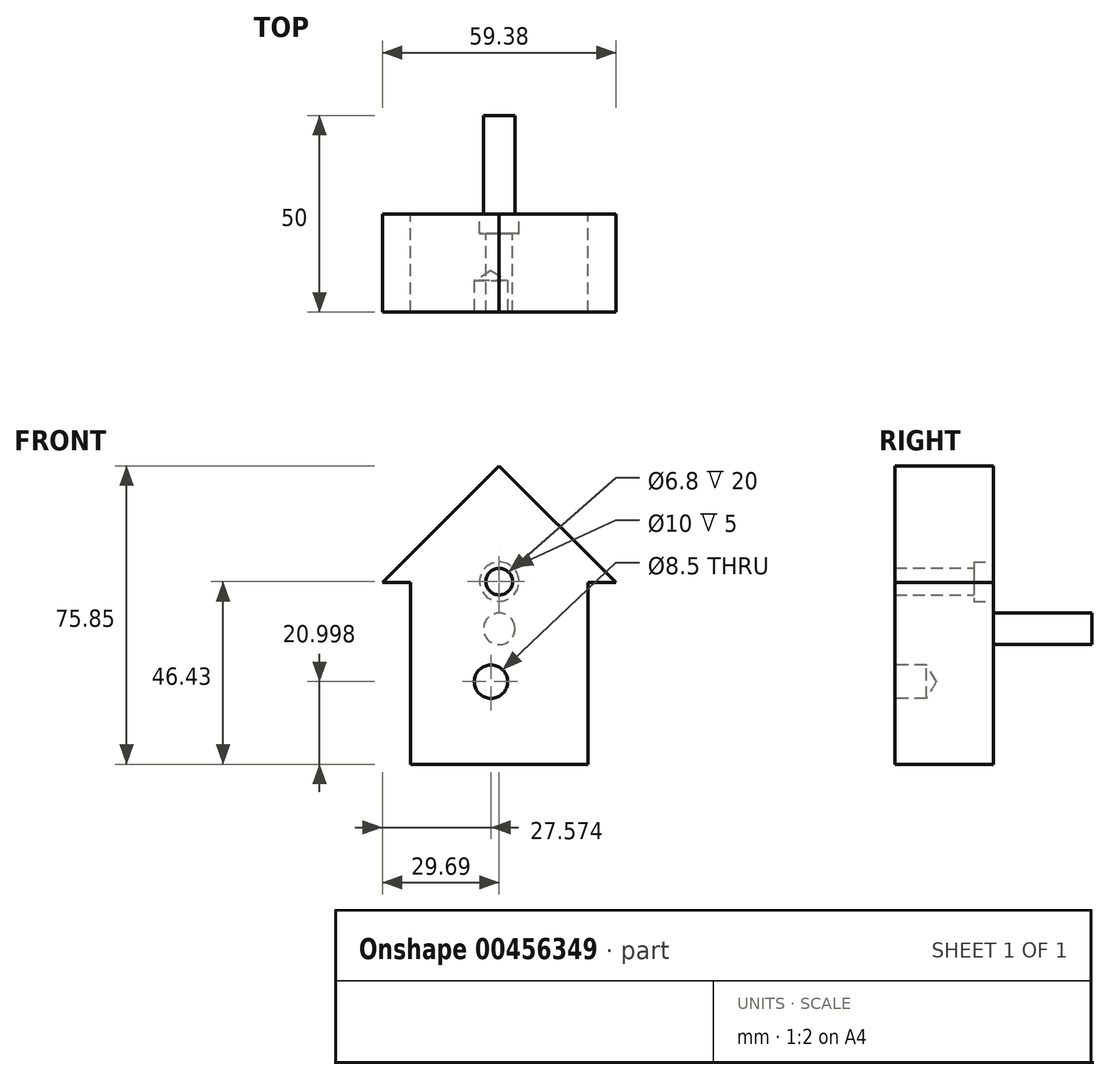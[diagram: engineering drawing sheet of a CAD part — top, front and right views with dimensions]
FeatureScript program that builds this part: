
annotation { "Feature Type Name" : "Feature", "Feature Type Description" : "" }
export const myFeature = defineFeature(function(context is Context, id is Id, definition is map)
    precondition{}
    {
        {
            var Q0;
            Q0=qCreatedBy(makeId("Front.planeOp"),FACE);
            var sketch = newSketch(context, id + "F0", { "sketchPlane" : qUnion([Q0])});
            skLineSegment(sketch, "E0", {"start": v(-22.57, -26.69) * mm, "end": v(22.57, -26.69) * mm});
            skLineSegment(sketch, "E1", {"start": v(22.57, -26.69) * mm, "end": v(22.57, 19.47) * mm});
            skLineSegment(sketch, "E2", {"start": v(22.57, 19.47) * mm, "end": v(29.69, 19.47) * mm});
            skLineSegment(sketch, "E3", {"start": v(29.69, 19.47) * mm, "end": v(0, 49.16) * mm});
            skLineSegment(sketch, "E4", {"start": v(0, 49.16) * mm, "end": v(-29.69, 19.47) * mm});
            skLineSegment(sketch, "E5", {"start": v(-29.69, 19.47) * mm, "end": v(-22.57, 19.47) * mm});
            skLineSegment(sketch, "E6", {"start": v(-22.57, 19.47) * mm, "end": v(-22.57, -26.69) * mm});
            skSolve(sketch);
        }
        {
            var Q0;
            Q0 = qSketchRegion(id + "F0", true);
            extrude(context, id + "F1", {"entities" : qUnion([Q0]), "depth" : 25 * mm});
        }
        {
            var Q0;
            Q0=makeQuery(id+"F1.opExtrude","CAP_FACE",FACE,{"disambiguationData":[OSD([sQuery(id+"F0.wireOp",EDGE,"E0"),sQuery(id+"F0.wireOp",EDGE,"E1"),sQuery(id+"F0.wireOp",EDGE,"E2"),sQuery(id+"F0.wireOp",EDGE,"E3"),sQuery(id+"F0.wireOp",EDGE,"E4"),sQuery(id+"F0.wireOp",EDGE,"E5"),sQuery(id+"F0.wireOp",EDGE,"E6")])],"isStart":true});
            var sketch = newSketch(context, id + "F2", { "sketchPlane" : qUnion([Q0])});
            skCircle(sketch, "E7", {"center": v(0, 7.72) * mm, "radius": 4 * mm});
            skSolve(sketch);
        }
        {
            var Q0;
            Q0 = qSketchRegion(id + "F2", true);
            extrude(context, id + "F3", {"entities" : qUnion([Q0]), "operationType" : NewBodyOperationType.ADD, "depth" : 25 * mm});
        }
        {
            var Q0;
            Q0=makeQuery(id+"F1.opExtrude","CAP_FACE",FACE,{"disambiguationData":[OSD([sQuery(id+"F0.wireOp",EDGE,"E0"),sQuery(id+"F0.wireOp",EDGE,"E1"),sQuery(id+"F0.wireOp",EDGE,"E2"),sQuery(id+"F0.wireOp",EDGE,"E3"),sQuery(id+"F0.wireOp",EDGE,"E4"),sQuery(id+"F0.wireOp",EDGE,"E5"),sQuery(id+"F0.wireOp",EDGE,"E6")])],"isStart":true});
            var sketch = newSketch(context, id + "F4", { "sketchPlane" : qUnion([Q0])});
            skCircle(sketch, "E8", {"center": v(0, 19.74) * mm, "radius": 7.9 * mm});
            skSolve(sketch);
        }
        {
            var Q0;
            Q0=sQuery(id+"F4.wireOp",VERTEX,"E8.center");
            var Q1;
            Q1=makeQuery(id+"F1.opExtrude","SWEPT_BODY",BODY,{"disambiguationData":[OSD([sQuery(id+"F0.wireOp",EDGE,"E0"),sQuery(id+"F0.wireOp",EDGE,"E1"),sQuery(id+"F0.wireOp",EDGE,"E2"),sQuery(id+"F0.wireOp",EDGE,"E3"),sQuery(id+"F0.wireOp",EDGE,"E4"),sQuery(id+"F0.wireOp",EDGE,"E5"),sQuery(id+"F0.wireOp",EDGE,"E6")])]});
            hole(context, id + "F5", {"style" : HoleStyle.C_BORE, "endStyle" : HoleEndStyle.THROUGH, "holeDiameter" : 6.8 * mm, "cBoreDiameter" : 10 * mm, "cBoreDepth" : 5 * mm, "majorDiameter" : 5 * mm, "isTappedThrough" : true, "tappedDepth" : 12 * mm, "tapClearance" : 3, "locations" : qUnion([Q0]), "scope" : qUnion([Q1])});
        }
        {
            var Q0;
            Q0=makeQuery(id+"F1.opExtrude","CAP_FACE",FACE,{"disambiguationData":[OSD([sQuery(id+"F0.wireOp",EDGE,"E0"),sQuery(id+"F0.wireOp",EDGE,"E1"),sQuery(id+"F0.wireOp",EDGE,"E2"),sQuery(id+"F0.wireOp",EDGE,"E3"),sQuery(id+"F0.wireOp",EDGE,"E4"),sQuery(id+"F0.wireOp",EDGE,"E5"),sQuery(id+"F0.wireOp",EDGE,"E6")])],"isStart":false});
            var sketch = newSketch(context, id + "F6", { "sketchPlane" : qUnion([Q0])});
            skCircle(sketch, "E9", {"center": v(-2.12, -5.7) * mm, "radius": 6 * mm});
            skCircle(sketch, "E10", {"center": v(-13.43, 9) * mm, "radius": 4.63 * mm});
            skSolve(sketch);
        }
        {
            var Q0;
            Q0=sQuery(id+"F6.wireOp",VERTEX,"E9.center");
            var Q1;
            Q1=makeQuery(id+"F1.opExtrude","SWEPT_BODY",BODY,{"disambiguationData":[OSD([sQuery(id+"F0.wireOp",EDGE,"E0"),sQuery(id+"F0.wireOp",EDGE,"E1"),sQuery(id+"F0.wireOp",EDGE,"E2"),sQuery(id+"F0.wireOp",EDGE,"E3"),sQuery(id+"F0.wireOp",EDGE,"E4"),sQuery(id+"F0.wireOp",EDGE,"E5"),sQuery(id+"F0.wireOp",EDGE,"E6")])]});
            hole(context, id + "F7", {"style" : HoleStyle.C_SINK, "endStyle" : HoleEndStyle.BLIND, "holeDiameter" : 8.5 * mm, "cSinkDiameter" : 8.5 * mm, "cSinkAngle" : 82 * degree, "majorDiameter" : 5 * mm, "holeDepth" : 8 * mm, "isTappedThrough" : true, "tappedDepth" : 12 * mm, "tapClearance" : 3, "locations" : qUnion([Q0]), "scope" : qUnion([Q1])});
        }
    });
